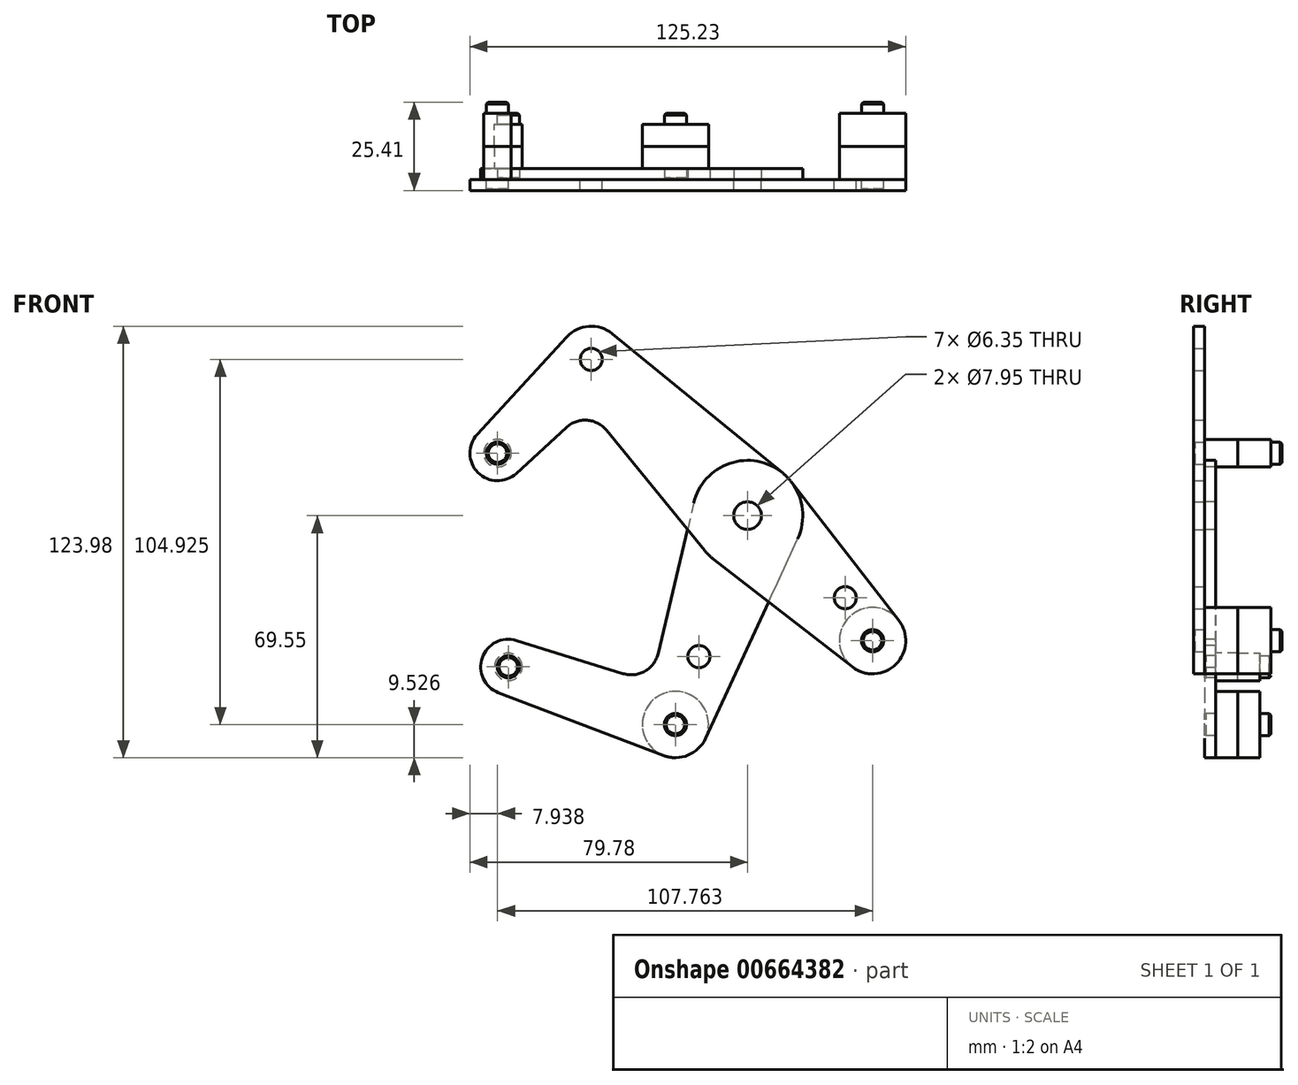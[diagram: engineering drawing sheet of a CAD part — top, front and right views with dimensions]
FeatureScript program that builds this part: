
annotation { "Feature Type Name" : "Feature", "Feature Type Description" : "" }
export const myFeature = defineFeature(function(context is Context, id is Id, definition is map)
    precondition{}
    {
        {
            var Q0;
            Q0=qCreatedBy(makeId("Front.planeOp"),FACE);
            var sketch = newSketch(context, id + "F0", { "sketchPlane" : qUnion([Q0])});
            skCircle(sketch, "E0", {"center": v(0, 0) * mm, "radius": 3.98 * mm});
            skCircle(sketch, "E1", {"center": v(0, 0) * mm, "radius": 15.88 * mm});
            skLineSegment(sketch, "E2", {"start": v(-44.9, 44.9) * mm, "end": v(35.92, -35.92) * mm, "construction": true});
            skCircle(sketch, "E3", {"center": v(35.92, -35.92) * mm, "radius": 3.18 * mm});
            skCircle(sketch, "E4", {"center": v(35.92, -35.92) * mm, "radius": 9.53 * mm});
            skCircle(sketch, "E5", {"center": v(-44.9, 44.9) * mm, "radius": 3.18 * mm});
            skCircle(sketch, "E6", {"center": v(-44.9, 44.9) * mm, "radius": 9.53 * mm});
            skCircle(sketch, "E7", {"center": v(0, 0) * mm, "radius": 3.18 * mm});
            skCircle(sketch, "E8", {"center": v(28.07, -23.58) * mm, "radius": 3.18 * mm});
            skLineSegment(sketch, "E9", {"start": v(-44.9, 44.9) * mm, "end": v(-71.84, 17.96) * mm, "construction": true});
            skCircle(sketch, "E10", {"center": v(-71.84, 17.96) * mm, "radius": 3.18 * mm});
            skCircle(sketch, "E11", {"center": v(-71.84, 17.96) * mm, "radius": 7.94 * mm});
            skPoint(sketch, "E12", {"position": v(25.83, -25.83) * mm});
            skLineSegment(sketch, "E13", {"start": v(-9.73, -12.54) * mm, "end": v(30.08, -43.45) * mm});
            skLineSegment(sketch, "E14", {"start": v(12.54, 9.73) * mm, "end": v(43.45, -30.08) * mm});
            skLineSegment(sketch, "E15", {"start": v(-77.68, 23.33) * mm, "end": v(-51.91, 51.35) * mm});
            skLineSegment(sketch, "E16", {"start": v(-38.87, 52.28) * mm, "end": v(10.05, 12.3) * mm});
            skLineSegment(sketch, "E17", {"start": v(-66.47, 12.12) * mm, "end": v(-52.09, 25.35) * mm});
            skLineSegment(sketch, "E18", {"start": v(-12.3, -10.05) * mm, "end": v(-40.55, 24.53) * mm});
            skArc(sketch, "E19", {"start": v(-52.09, 25.35) * mm, "mid": v(-46.14, 27.43) * mm, "end": v(-40.55, 24.53) * mm});
            skLineSegment(sketch, "E20", {"start": v(0, 0) * mm, "end": v(-20.72, -60.02) * mm, "construction": true});
            skLineSegment(sketch, "E21", {"start": v(-20.72, -60.02) * mm, "end": v(-68.74, -43.45) * mm, "construction": true});
            skCircle(sketch, "E22", {"center": v(-13.98, -40.5) * mm, "radius": 3.18 * mm});
            skCircle(sketch, "E23", {"center": v(-20.72, -60.02) * mm, "radius": 3.18 * mm});
            skCircle(sketch, "E24", {"center": v(-20.72, -60.02) * mm, "radius": 9.53 * mm});
            skCircle(sketch, "E25", {"center": v(-68.74, -43.45) * mm, "radius": 3.18 * mm});
            skCircle(sketch, "E26", {"center": v(-68.74, -43.45) * mm, "radius": 7.94 * mm});
            skLineSegment(sketch, "E27", {"start": v(-71.57, -50.86) * mm, "end": v(-24.11, -68.93) * mm});
            skLineSegment(sketch, "E28", {"start": v(-12.08, -64.02) * mm, "end": v(14.41, -6.66) * mm});
            skLineSegment(sketch, "E29", {"start": v(-66.39, -35.87) * mm, "end": v(-35.78, -45.37) * mm});
            skLineSegment(sketch, "E30", {"start": v(-15.45, 3.65) * mm, "end": v(-25.68, -39.61) * mm});
            skArc(sketch, "E31", {"start": v(-35.78, -45.37) * mm, "mid": v(-29.48, -44.69) * mm, "end": v(-25.68, -39.61) * mm});
            skSolve(sketch);
        }
        {
            var Q0;
            Q0=qCreatedBy(makeId("Front.planeOp"),FACE);
            cPlane(context, id + "F1", {"entities" : qUnion([Q0]), "cplaneType" : CPlaneType.OFFSET, "offset" : 9.52 * mm, "oppositeDirection" : true, "width" : 152.4 * mm, "height" : 152.4 * mm});
        }
        {
            var Q0;
            Q0=makeQuery(id+"F0.imprint","IMPRINT",FACE,{"disambiguationData":[TD([[makeQuery(id+"F0.imprint","IMPRINT",EDGE,{"derivedFrom":sQuery(id+"F0.wireOp",EDGE,"E3")}),-1.0]])]});
            var Q1;
            Q1=makeQuery(id+"F0.imprint","IMPRINT",FACE,{"disambiguationData":[TD([[makeQuery(id+"F0.imprint","IMPRINT",EDGE,{"derivedFrom":sQuery(id+"F0.wireOp",EDGE,"E5")}),-1.0]])]});
            var Q2;
            Q2=makeQuery(id+"F0.imprint","IMPRINT",FACE,{"disambiguationData":[TD([[makeQuery(id+"F0.imprint","IMPRINT",EDGE,{"derivedFrom":sQuery(id+"F0.wireOp",EDGE,"E10")}),-1.0]])]});
            var Q3;
            {var subQ0=sQuery(id+"F0.wireOp",EDGE,"E18");var subQ1=sQuery(id+"F0.wireOp",EDGE,"E1");var subQ2=makeQuery(id+"F0.imprint","INTERSECT",VERTEX,{"derivedFrom":[subQ1,subQ0]});Q3=makeQuery(id+"F0.imprint","IMPRINT",FACE,{"disambiguationData":[TD([[makeQuery(id+"F0.imprint","IMPRINT",EDGE,{"disambiguationData":[TD([[subQ2,1.0]])],"derivedFrom":subQ1}),-1.0]])]});}
            var Q4;
            {var subQ0=sQuery(id+"F0.wireOp",EDGE,"E13");var subQ1=sQuery(id+"F0.wireOp",EDGE,"E1");var subQ2=makeQuery(id+"F0.imprint","INTERSECT",VERTEX,{"derivedFrom":[subQ1,subQ0]});Q4=makeQuery(id+"F0.imprint","IMPRINT",FACE,{"disambiguationData":[TD([[makeQuery(id+"F0.imprint","IMPRINT",EDGE,{"disambiguationData":[TD([[subQ2,-1.0]])],"derivedFrom":subQ1}),-1.0]])]});}
            var Q5;
            {var subQ0=sQuery(id+"F0.wireOp",EDGE,"E15");Q5=makeQuery(id+"F0.imprint","IMPRINT",FACE,{"disambiguationData":[TD([[makeQuery(id+"F0.imprint","IMPRINT",EDGE,{"derivedFrom":subQ0}),-1.0]])]});}
            var Q6;
            Q6=makeQuery(id+"F0.imprint","IMPRINT",FACE,{"disambiguationData":[TD([[makeQuery(id+"F0.imprint","IMPRINT",EDGE,{"derivedFrom":sQuery(id+"F0.wireOp",EDGE,"E8")}),-1.0]])]});
            var Q7;
            Q7=makeQuery(id+"F0.imprint","IMPRINT",FACE,{"disambiguationData":[TD([[makeQuery(id+"F0.imprint","IMPRINT",EDGE,{"derivedFrom":sQuery(id+"F0.wireOp",EDGE,"E0")}),-1.0]])]});
            extrude(context, id + "F2", {"entities" : qUnion([Q0, Q1, Q2, Q3, Q4, Q5, Q6, Q7]), "depth" : 3.17 * mm, "offsetDistance" : 25.4 * mm});
        }
        {
            var Q0;
            Q0=makeQuery(id+"F0.imprint","IMPRINT",FACE,{"disambiguationData":[TD([[makeQuery(id+"F0.imprint","IMPRINT",EDGE,{"derivedFrom":sQuery(id+"F0.wireOp",EDGE,"E25")}),-1.0]])]});
            var Q1;
            Q1=makeQuery(id+"F0.imprint","IMPRINT",FACE,{"disambiguationData":[TD([[makeQuery(id+"F0.imprint","IMPRINT",EDGE,{"derivedFrom":sQuery(id+"F0.wireOp",EDGE,"E0")}),-1.0]])]});
            var Q2;
            Q2=makeQuery(id+"F0.imprint","IMPRINT",FACE,{"disambiguationData":[TD([[makeQuery(id+"F0.imprint","IMPRINT",EDGE,{"derivedFrom":sQuery(id+"F0.wireOp",EDGE,"E23")}),-1.0]])]});
            var Q3;
            {var subQ0=sQuery(id+"F0.wireOp",EDGE,"E13");var subQ1=sQuery(id+"F0.wireOp",EDGE,"E1");var subQ2=makeQuery(id+"F0.imprint","INTERSECT",VERTEX,{"derivedFrom":[subQ1,subQ0]});Q3=makeQuery(id+"F0.imprint","IMPRINT",FACE,{"disambiguationData":[TD([[makeQuery(id+"F0.imprint","IMPRINT",EDGE,{"disambiguationData":[TD([[subQ2,-1.0]])],"derivedFrom":subQ1}),-1.0]])]});}
            var Q4;
            Q4=makeQuery(id+"F0.imprint","IMPRINT",FACE,{"disambiguationData":[TD([[makeQuery(id+"F0.imprint","IMPRINT",EDGE,{"derivedFrom":sQuery(id+"F0.wireOp",EDGE,"E22")}),-1.0]])]});
            var Q5;
            {var subQ0=sQuery(id+"F0.wireOp",EDGE,"E18");var subQ1=sQuery(id+"F0.wireOp",EDGE,"E1");var subQ2=makeQuery(id+"F0.imprint","INTERSECT",VERTEX,{"derivedFrom":[subQ1,subQ0]});Q5=makeQuery(id+"F0.imprint","IMPRINT",FACE,{"disambiguationData":[TD([[makeQuery(id+"F0.imprint","IMPRINT",EDGE,{"disambiguationData":[TD([[subQ2,1.0]])],"derivedFrom":subQ1}),-1.0]])]});}
            extrude(context, id + "F3", {"entities" : qUnion([Q0, Q1, Q2, Q3, Q4, Q5]), "oppositeDirection" : true, "depth" : 3.17 * mm, "offsetDistance" : 25.4 * mm});
        }
        {
            var Q0;
            Q0=makeQuery(id+"F2.opExtrude","CAP_FACE",FACE,{"disambiguationData":[OSD([sQuery(id+"F0.wireOp",EDGE,"E0"),sQuery(id+"F0.wireOp",EDGE,"E1"),sQuery(id+"F0.wireOp",EDGE,"E3"),sQuery(id+"F0.wireOp",EDGE,"E4"),sQuery(id+"F0.wireOp",EDGE,"E5"),sQuery(id+"F0.wireOp",EDGE,"E6"),sQuery(id+"F0.wireOp",EDGE,"E8"),sQuery(id+"F0.wireOp",EDGE,"E10"),sQuery(id+"F0.wireOp",EDGE,"E11"),sQuery(id+"F0.wireOp",EDGE,"E13"),sQuery(id+"F0.wireOp",EDGE,"E14"),sQuery(id+"F0.wireOp",EDGE,"E15"),sQuery(id+"F0.wireOp",EDGE,"E16"),sQuery(id+"F0.wireOp",EDGE,"E17"),sQuery(id+"F0.wireOp",EDGE,"E18"),sQuery(id+"F0.wireOp",EDGE,"E19")])],"isStart":false});
            var sketch = newSketch(context, id + "F4", { "sketchPlane" : qUnion([Q0])});
            skCircle(sketch, "E32", {"center": v(-71.84, 17.96) * mm, "radius": 3.97 * mm});
            skCircle(sketch, "E33", {"center": v(35.92, -35.92) * mm, "radius": 9.53 * mm});
            skSolve(sketch);
        }
        {
            var Q0;
            Q0=makeQuery(id+"F3.opExtrude","CAP_FACE",FACE,{"disambiguationData":[OSD([sQuery(id+"F0.wireOp",EDGE,"E0"),sQuery(id+"F0.wireOp",EDGE,"E1"),sQuery(id+"F0.wireOp",EDGE,"E22"),sQuery(id+"F0.wireOp",EDGE,"E23"),sQuery(id+"F0.wireOp",EDGE,"E24"),sQuery(id+"F0.wireOp",EDGE,"E25"),sQuery(id+"F0.wireOp",EDGE,"E26"),sQuery(id+"F0.wireOp",EDGE,"E27"),sQuery(id+"F0.wireOp",EDGE,"E28"),sQuery(id+"F0.wireOp",EDGE,"E29"),sQuery(id+"F0.wireOp",EDGE,"E30"),sQuery(id+"F0.wireOp",EDGE,"E31")])],"isStart":true});
            var sketch = newSketch(context, id + "F5", { "sketchPlane" : qUnion([Q0])});
            skCircle(sketch, "E34", {"center": v(-20.72, -60.02) * mm, "radius": 9.53 * mm});
            skCircle(sketch, "E35", {"center": v(-68.74, -43.45) * mm, "radius": 3.97 * mm});
            skSolve(sketch);
        }
        {
            var Q0;
            Q0=qSketchRegion(id+"F4",true);
            var Q1;
            Q1=qSketchRegion(id+"F5",true);
            var Q2;
            Q2=qCreatedBy(id+"F1.planeOp",FACE);
            extrude(context, id + "F6", {"entities" : qUnion([Q0, Q1]), "endBound" : BoundingType.UP_TO_SURFACE, "oppositeDirection" : true, "depth" : 25.4 * mm, "endBoundEntityFace" : qUnion([Q2]), "offsetDistance" : 25.4 * mm});
        }
        {
            var Q0;
            Q0=makeQuery(id+"F2.opExtrude","SWEPT_BODY",BODY,{"disambiguationData":[OSD([sQuery(id+"F0.wireOp",EDGE,"E0"),sQuery(id+"F0.wireOp",EDGE,"E1"),sQuery(id+"F0.wireOp",EDGE,"E3"),sQuery(id+"F0.wireOp",EDGE,"E4"),sQuery(id+"F0.wireOp",EDGE,"E5"),sQuery(id+"F0.wireOp",EDGE,"E6"),sQuery(id+"F0.wireOp",EDGE,"E8"),sQuery(id+"F0.wireOp",EDGE,"E10"),sQuery(id+"F0.wireOp",EDGE,"E11"),sQuery(id+"F0.wireOp",EDGE,"E13"),sQuery(id+"F0.wireOp",EDGE,"E14"),sQuery(id+"F0.wireOp",EDGE,"E15"),sQuery(id+"F0.wireOp",EDGE,"E16"),sQuery(id+"F0.wireOp",EDGE,"E17"),sQuery(id+"F0.wireOp",EDGE,"E18"),sQuery(id+"F0.wireOp",EDGE,"E19")])]});
            var Q1;
            Q1=makeQuery(id+"F3.opExtrude","SWEPT_BODY",BODY,{"disambiguationData":[OSD([sQuery(id+"F0.wireOp",EDGE,"E0"),sQuery(id+"F0.wireOp",EDGE,"E1"),sQuery(id+"F0.wireOp",EDGE,"E22"),sQuery(id+"F0.wireOp",EDGE,"E23"),sQuery(id+"F0.wireOp",EDGE,"E24"),sQuery(id+"F0.wireOp",EDGE,"E25"),sQuery(id+"F0.wireOp",EDGE,"E26"),sQuery(id+"F0.wireOp",EDGE,"E27"),sQuery(id+"F0.wireOp",EDGE,"E28"),sQuery(id+"F0.wireOp",EDGE,"E29"),sQuery(id+"F0.wireOp",EDGE,"E30"),sQuery(id+"F0.wireOp",EDGE,"E31")])]});
            var Q2;
            Q2=makeQuery(id+"F6.opExtrude","SWEPT_BODY",BODY,{"disambiguationData":[OSD([sQuery(id+"F4.wireOp",EDGE,"E32")])]});
            var Q3;
            Q3=makeQuery(id+"F6.opExtrude","SWEPT_BODY",BODY,{"disambiguationData":[OSD([sQuery(id+"F4.wireOp",EDGE,"E33")])]});
            var Q4;
            Q4=makeQuery(id+"F6.opExtrude","SWEPT_BODY",BODY,{"disambiguationData":[OSD([sQuery(id+"F5.wireOp",EDGE,"E34")])]});
            var Q5;
            Q5=makeQuery(id+"F6.opExtrude","SWEPT_BODY",BODY,{"disambiguationData":[OSD([sQuery(id+"F5.wireOp",EDGE,"E35")])]});
            booleanBodies(context, id + "F7", {"operationType" : BooleanOperationType.SUBTRACTION, "tools" : qUnion([Q0, Q1]), "targets" : qUnion([Q2, Q3, Q4, Q5]), "keepTools" : true});
        }
        {
            var Q0;
            Q0=makeQuery(id+"F6.opExtrude","CAP_FACE",FACE,{"disambiguationData":[OSD([sQuery(id+"F4.wireOp",EDGE,"E32")])],"isStart":true});
            var Q1;
            Q1=makeQuery(id+"F6.opExtrude","CAP_FACE",FACE,{"disambiguationData":[OSD([sQuery(id+"F5.wireOp",EDGE,"E35")])],"isStart":true});
            var Q2;
            Q2=makeQuery(id+"F6.opExtrude","CAP_FACE",FACE,{"disambiguationData":[OSD([sQuery(id+"F5.wireOp",EDGE,"E34")])],"isStart":true});
            var Q3;
            Q3=makeQuery(id+"F6.opExtrude","CAP_FACE",FACE,{"disambiguationData":[OSD([sQuery(id+"F4.wireOp",EDGE,"E33")])],"isStart":true});
            chamfer(context, id + "F8", {"entities" : qUnion([Q0, Q1, Q2, Q3]), "width" : 0.5 * mm, "tangentPropagation" : true});
        }
        {
            var Q0;
            Q0=makeQuery(id+"F6.opExtrude","SWEPT_BODY",BODY,{"disambiguationData":[OSD([sQuery(id+"F4.wireOp",EDGE,"E33")])]});
            var Q1;
            Q1=makeQuery(id+"F6.opExtrude","SWEPT_BODY",BODY,{"disambiguationData":[OSD([sQuery(id+"F4.wireOp",EDGE,"E32")])]});
            var Q2;
            Q2=makeQuery(id+"F6.opExtrude","SWEPT_BODY",BODY,{"disambiguationData":[OSD([sQuery(id+"F5.wireOp",EDGE,"E34")])]});
            var Q3;
            Q3=makeQuery(id+"F6.opExtrude","SWEPT_BODY",BODY,{"disambiguationData":[OSD([sQuery(id+"F5.wireOp",EDGE,"E35")])]});
            var Q4;
            Q4=qCreatedBy(id+"F1.planeOp",FACE);
            mirror(context, id + "F9", {"entities" : qUnion([Q0, Q1, Q2, Q3]), "mirrorPlane" : qUnion([Q4])});
        }
    });
